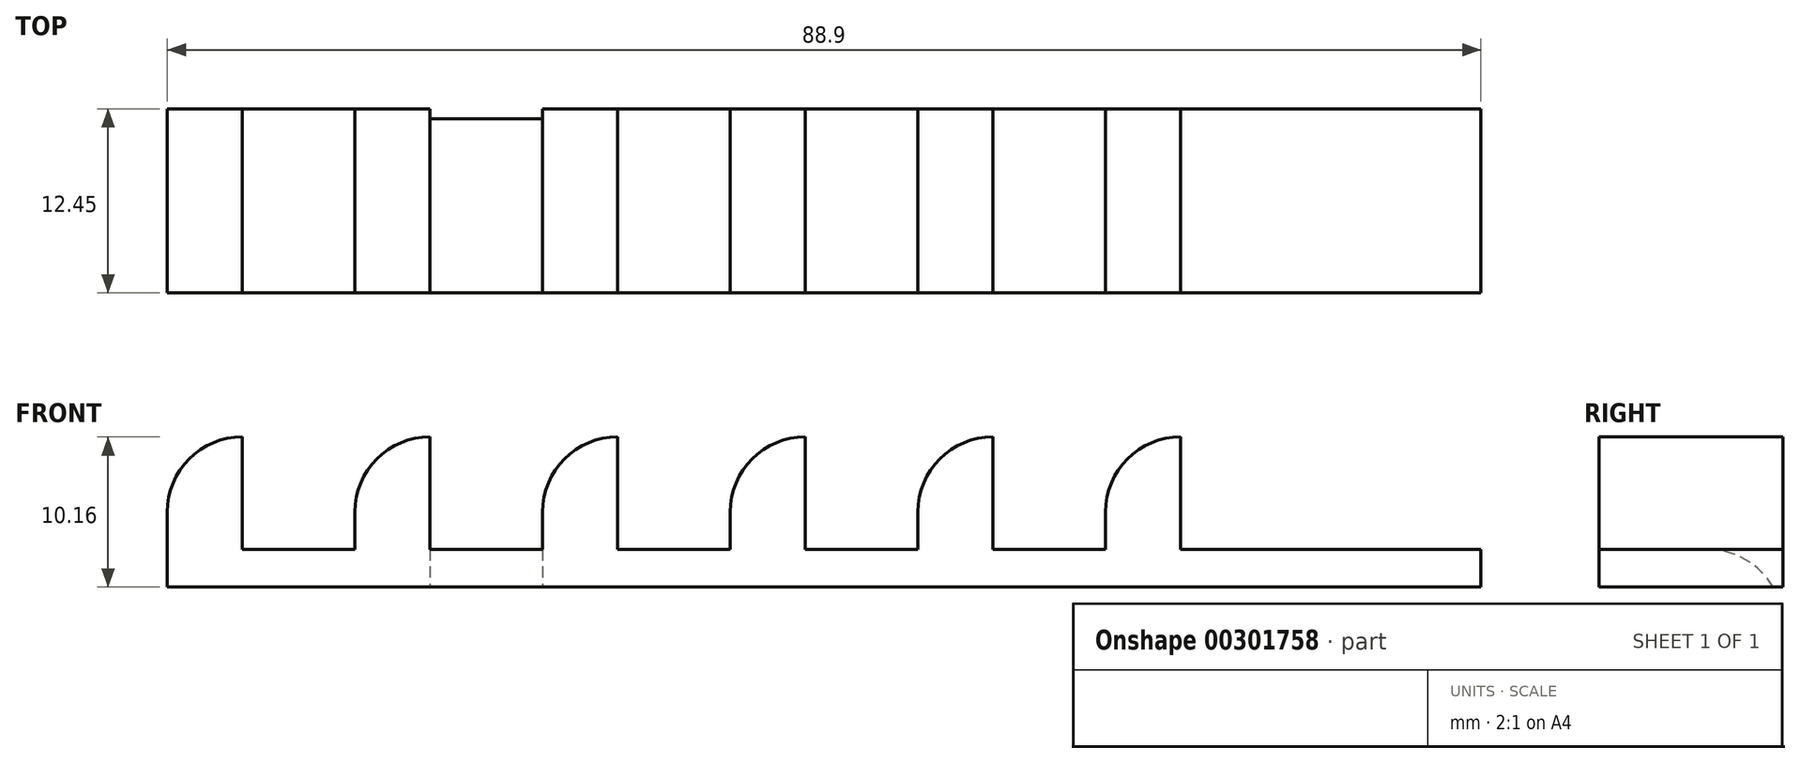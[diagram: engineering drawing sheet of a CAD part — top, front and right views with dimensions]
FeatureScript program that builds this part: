
annotation { "Feature Type Name" : "Feature", "Feature Type Description" : "" }
export const myFeature = defineFeature(function(context is Context, id is Id, definition is map)
    precondition{}
    {
        {
            var Q0;
            Q0=qCreatedBy(makeId("Top.planeOp"),FACE);
            var sketch = newSketch(context, id + "F0", { "sketchPlane" : qUnion([Q0])});
            skLineSegment(sketch, "E0.bottom", {"start": v(-48.45, -38.2) * mm, "end": v(40.45, -38.2) * mm});
            skLineSegment(sketch, "E0.top", {"start": v(-48.45, -25.76) * mm, "end": v(40.45, -25.76) * mm});
            skLineSegment(sketch, "E0.left", {"start": v(-48.45, -38.2) * mm, "end": v(-48.45, -25.76) * mm});
            skLineSegment(sketch, "E0.right", {"start": v(40.45, -38.2) * mm, "end": v(40.45, -25.76) * mm});
            skSolve(sketch);
        }
        {
            var Q0;
            Q0 = qSketchRegion(id + "F0", true);
            extrude(context, id + "F1", {"entities" : qUnion([Q0]), "depth" : 2.54 * mm});
        }
        {
            var Q0;
            Q0=makeQuery(id+"F1.opExtrude","CAP_FACE",FACE,{"disambiguationData":[OSD([sQuery(id+"F0.wireOp",EDGE,"E0.bottom"),sQuery(id+"F0.wireOp",EDGE,"E0.top"),sQuery(id+"F0.wireOp",EDGE,"E0.left"),sQuery(id+"F0.wireOp",EDGE,"E0.right")])],"isStart":false});
            var sketch = newSketch(context, id + "F2", { "sketchPlane" : qUnion([Q0])});
            skLineSegment(sketch, "E1.bottom", {"start": v(-48.45, -38.2) * mm, "end": v(-43.37, -38.2) * mm});
            skLineSegment(sketch, "E1.top", {"start": v(-48.45, -25.76) * mm, "end": v(-43.37, -25.76) * mm});
            skLineSegment(sketch, "E1.left", {"start": v(-48.45, -38.2) * mm, "end": v(-48.45, -25.76) * mm});
            skLineSegment(sketch, "E1.right", {"start": v(-43.37, -38.2) * mm, "end": v(-43.37, -25.76) * mm});
            skLineSegment(sketch, "E2.bottom", {"start": v(-35.75, -38.2) * mm, "end": v(-30.67, -38.2) * mm});
            skLineSegment(sketch, "E2.top", {"start": v(-35.75, -25.76) * mm, "end": v(-30.67, -25.76) * mm});
            skLineSegment(sketch, "E2.left", {"start": v(-35.75, -38.2) * mm, "end": v(-35.75, -25.76) * mm});
            skLineSegment(sketch, "E2.right", {"start": v(-30.67, -38.2) * mm, "end": v(-30.67, -25.76) * mm});
            skLineSegment(sketch, "E3.bottom", {"start": v(-23.05, -38.2) * mm, "end": v(-17.97, -38.2) * mm});
            skLineSegment(sketch, "E3.top", {"start": v(-23.05, -25.76) * mm, "end": v(-17.97, -25.76) * mm});
            skLineSegment(sketch, "E3.left", {"start": v(-23.05, -38.2) * mm, "end": v(-23.05, -25.76) * mm});
            skLineSegment(sketch, "E3.right", {"start": v(-17.97, -38.2) * mm, "end": v(-17.97, -25.76) * mm});
            skLineSegment(sketch, "E4.bottom", {"start": v(-10.35, -38.2) * mm, "end": v(-5.27, -38.2) * mm});
            skLineSegment(sketch, "E4.top", {"start": v(-10.35, -25.76) * mm, "end": v(-5.27, -25.76) * mm});
            skLineSegment(sketch, "E4.left", {"start": v(-10.35, -38.2) * mm, "end": v(-10.35, -25.76) * mm});
            skLineSegment(sketch, "E4.right", {"start": v(-5.27, -38.2) * mm, "end": v(-5.27, -25.76) * mm});
            skLineSegment(sketch, "E5.bottom", {"start": v(2.35, -38.2) * mm, "end": v(7.43, -38.2) * mm});
            skLineSegment(sketch, "E5.top", {"start": v(2.35, -25.76) * mm, "end": v(7.43, -25.76) * mm});
            skLineSegment(sketch, "E5.left", {"start": v(2.35, -38.2) * mm, "end": v(2.35, -25.76) * mm});
            skLineSegment(sketch, "E5.right", {"start": v(7.43, -38.2) * mm, "end": v(7.43, -25.76) * mm});
            skLineSegment(sketch, "E6.bottom", {"start": v(15.05, -38.2) * mm, "end": v(20.13, -38.2) * mm});
            skLineSegment(sketch, "E6.top", {"start": v(15.05, -25.76) * mm, "end": v(20.13, -25.76) * mm});
            skLineSegment(sketch, "E6.left", {"start": v(15.05, -38.2) * mm, "end": v(15.05, -25.76) * mm});
            skLineSegment(sketch, "E6.right", {"start": v(20.13, -38.2) * mm, "end": v(20.13, -25.76) * mm});
            skSolve(sketch);
        }
        {
            var Q0;
            Q0 = qSketchRegion(id + "F2", true);
            extrude(context, id + "F3", {"entities" : qUnion([Q0]), "operationType" : NewBodyOperationType.ADD, "depth" : 7.62 * mm});
        }
        {
            var Q0;
            Q0=makeQuery(id+"F3.opExtrude","CAP_EDGE",EDGE,{"disambiguationData":[OSD([sQuery(id+"F2.wireOp",EDGE,"E1.left")])],"isStart":false});
            var Q1;
            Q1=makeQuery(id+"F3.opExtrude","CAP_EDGE",EDGE,{"disambiguationData":[OSD([sQuery(id+"F2.wireOp",EDGE,"E2.left")])],"isStart":false});
            var Q2;
            {var subQ0=sQuery(id+"F0.wireOp",EDGE,"E0.top");Q2=makeQuery(id+"F3.boolean.opBoolean","SPLIT",EDGE,{"disambiguationData":[TD([makeQuery(id+"F3.opExtrude","SWEPT_FACE",FACE,{"disambiguationData":[OSD([sQuery(id+"F2.wireOp",EDGE,"E2.right")])]})])],"derivedFrom":makeQuery(id+"F1.opExtrude","CAP_EDGE",EDGE,{"disambiguationData":[OSD([subQ0])],"isStart":false})});}
            var Q3;
            Q3=makeQuery(id+"F3.opExtrude","CAP_EDGE",EDGE,{"disambiguationData":[OSD([sQuery(id+"F2.wireOp",EDGE,"E3.left")])],"isStart":false});
            var Q4;
            Q4=makeQuery(id+"F3.opExtrude","CAP_EDGE",EDGE,{"disambiguationData":[OSD([sQuery(id+"F2.wireOp",EDGE,"E4.left")])],"isStart":false});
            var Q5;
            Q5=makeQuery(id+"F3.opExtrude","CAP_EDGE",EDGE,{"disambiguationData":[OSD([sQuery(id+"F2.wireOp",EDGE,"E5.left")])],"isStart":false});
            var Q6;
            Q6=makeQuery(id+"F3.opExtrude","CAP_EDGE",EDGE,{"disambiguationData":[OSD([sQuery(id+"F2.wireOp",EDGE,"E6.left")])],"isStart":false});
            fillet(context, id + "F4", {"entities" : qUnion([Q0, Q1, Q2, Q3, Q4, Q5, Q6]), "radius" : 5.08 * mm, "tangentPropagation" : true, "allowEdgeOverflow" : false});
        }
    });
